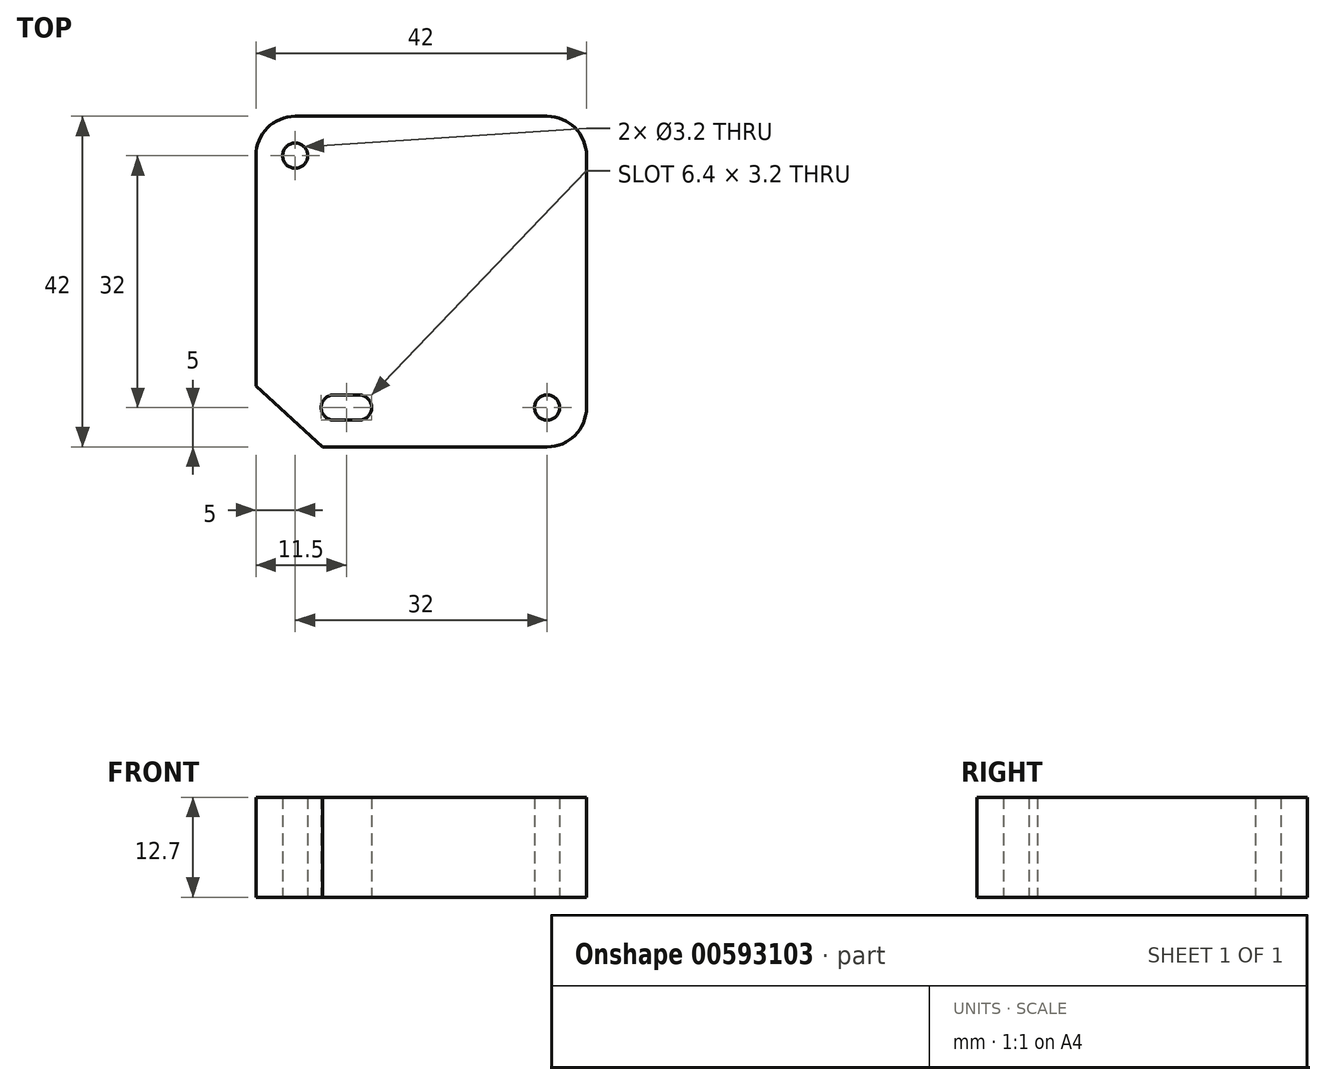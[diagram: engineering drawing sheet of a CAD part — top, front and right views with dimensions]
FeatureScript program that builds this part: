
annotation { "Feature Type Name" : "Feature", "Feature Type Description" : "" }
export const myFeature = defineFeature(function(context is Context, id is Id, definition is map)
    precondition{}
    {
        {
            var Q0;
            Q0=qCreatedBy(makeId("Top.planeOp"),FACE);
            var sketch = newSketch(context, id + "F0", { "sketchPlane" : qUnion([Q0])});
            skLineSegment(sketch, "E0.bottom", {"start": v(16, 21) * mm, "end": v(-16, 21) * mm});
            skLineSegment(sketch, "E0.top", {"start": v(16, -21) * mm, "end": v(-12.54, -21) * mm});
            skLineSegment(sketch, "E0.left", {"start": v(21, 16) * mm, "end": v(21, -16) * mm});
            skLineSegment(sketch, "E0.right", {"start": v(-21, 16) * mm, "end": v(-21, -13.28) * mm});
            skPoint(sketch, "E0.middle", {"position": v(0, 0) * mm});
            skPoint(sketch, "E1.visualSharp", {"position": v(-21, 21) * mm});
            skArc(sketch, "E1.filletArc", {"start": v(-16, 21) * mm, "mid": v(-19.54, 19.54) * mm, "end": v(-21, 16) * mm});
            skPoint(sketch, "E2.visualSharp", {"position": v(21, 21) * mm});
            skArc(sketch, "E2.filletArc", {"start": v(21, 16) * mm, "mid": v(19.54, 19.54) * mm, "end": v(16, 21) * mm});
            skPoint(sketch, "E3.visualSharp", {"position": v(21, -21) * mm});
            skArc(sketch, "E3.filletArc", {"start": v(16, -21) * mm, "mid": v(19.54, -19.54) * mm, "end": v(21, -16) * mm});
            skLineSegment(sketch, "E4", {"start": v(-21, -13.28) * mm, "end": v(-12.54, -21) * mm});
            skPoint(sketch, "E5.orphan", {"position": v(-21, -21) * mm});
            skCircle(sketch, "E6", {"center": v(-16, 16) * mm, "radius": 1.6 * mm});
            skCircle(sketch, "E7", {"center": v(16, -16) * mm, "radius": 1.6 * mm});
            skArc(sketch, "E8", {"start": v(-11.1, -14.4) * mm, "mid": v(-12.7, -16) * mm, "end": v(-11.1, -17.6) * mm});
            skArc(sketch, "E9", {"start": v(-7.9, -17.6) * mm, "mid": v(-6.3, -16) * mm, "end": v(-7.9, -14.4) * mm});
            skLineSegment(sketch, "E10", {"start": v(-11.1, -14.4) * mm, "end": v(-7.9, -14.4) * mm});
            skLineSegment(sketch, "E11", {"start": v(-7.9, -17.6) * mm, "end": v(-11.1, -17.6) * mm});
            skSolve(sketch);
        }
        {
            var Q0;
            Q0=makeQuery(id+"F0.imprint","IMPRINT",FACE,{"disambiguationData":[TD([[makeQuery(id+"F0.imprint","IMPRINT",EDGE,{"derivedFrom":sQuery(id+"F0.wireOp",EDGE,"E0.bottom")}),1.0]])]});
            extrude(context, id + "F1", {"entities" : qUnion([Q0]), "depth" : 12.7 * mm, "offsetDistance" : 25 * mm});
        }
    });
